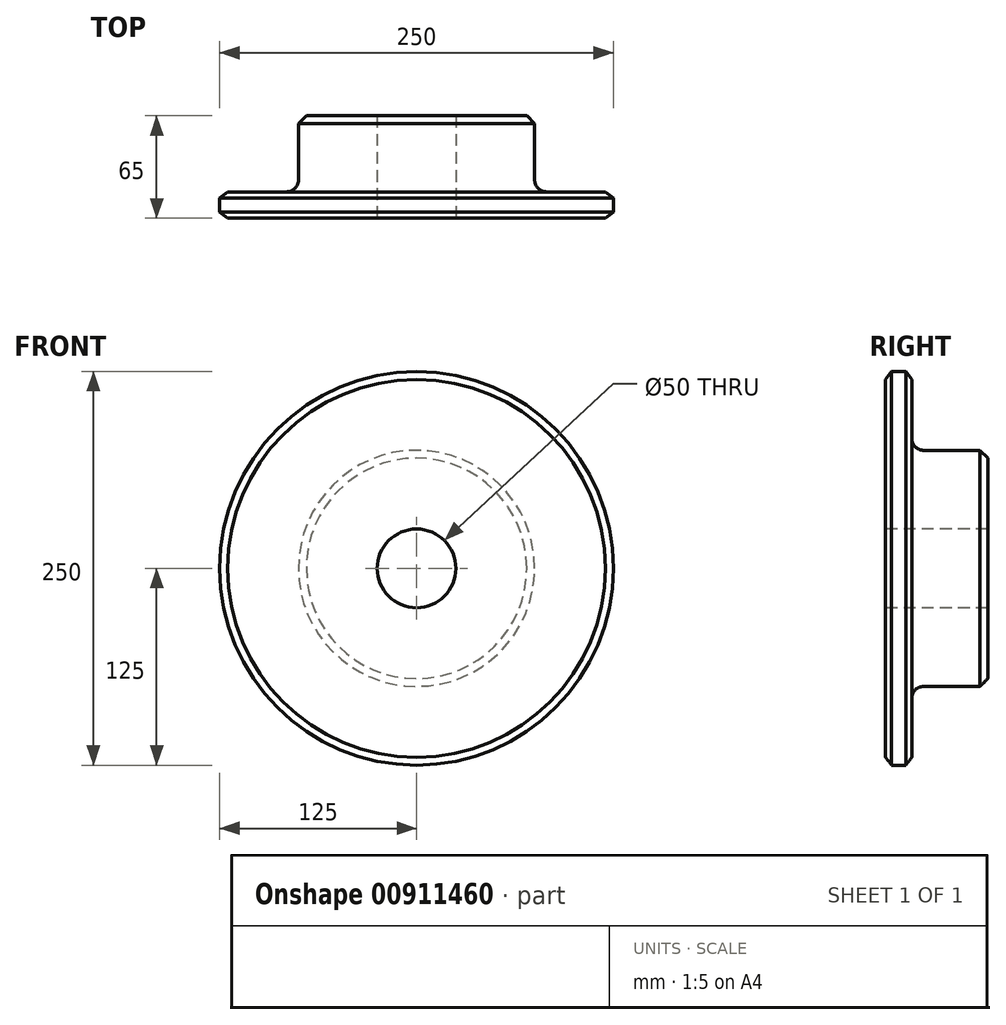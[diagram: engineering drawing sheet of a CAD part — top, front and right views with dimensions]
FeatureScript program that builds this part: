
annotation { "Feature Type Name" : "Feature", "Feature Type Description" : "" }
export const myFeature = defineFeature(function(context is Context, id is Id, definition is map)
    precondition{}
    {
        {
            var Q0;
            Q0=qCreatedBy(makeId("Right.planeOp"),FACE);
            var sketch = newSketch(context, id + "F0", { "sketchPlane" : qUnion([Q0])});
            skLineSegment(sketch, "E0", {"start": v(0, 0) * mm, "end": v(65, 0) * mm, "construction": true});
            skLineSegment(sketch, "E1.bottom", {"start": v(0, 25) * mm, "end": v(16.67, 25) * mm});
            skLineSegment(sketch, "E1.top", {"start": v(0, 125) * mm, "end": v(16.67, 125) * mm});
            skLineSegment(sketch, "E1.left", {"start": v(0, 25) * mm, "end": v(0, 125) * mm});
            skLineSegment(sketch, "E1.right", {"start": v(16.67, 25) * mm, "end": v(16.67, 125) * mm});
            skLineSegment(sketch, "E2.bottom", {"start": v(0, 25) * mm, "end": v(65, 25) * mm});
            skLineSegment(sketch, "E2.top", {"start": v(0, 75) * mm, "end": v(65, 75) * mm});
            skLineSegment(sketch, "E2.left", {"start": v(0, 25) * mm, "end": v(0, 75) * mm});
            skLineSegment(sketch, "E2.right", {"start": v(65, 25) * mm, "end": v(65, 75) * mm});
            skLineSegment(sketch, "E3.MirrorCS", {"start": v(0, -25) * mm, "end": v(16.67, -25) * mm});
            skLineSegment(sketch, "E4.MirrorCS", {"start": v(65, -25) * mm, "end": v(65, -75) * mm});
            skLineSegment(sketch, "E5.MirrorCS", {"start": v(0, -25) * mm, "end": v(65, -25) * mm});
            skLineSegment(sketch, "E6.MirrorCS", {"start": v(0, -25) * mm, "end": v(0, -75) * mm});
            skLineSegment(sketch, "E7.MirrorCS", {"start": v(0, -75) * mm, "end": v(65, -75) * mm});
            skLineSegment(sketch, "E8.MirrorCS", {"start": v(0, -25) * mm, "end": v(0, -125) * mm});
            skLineSegment(sketch, "E9.MirrorCS", {"start": v(16.67, -25) * mm, "end": v(16.67, -125) * mm});
            skLineSegment(sketch, "E10.MirrorCS", {"start": v(0, -125) * mm, "end": v(16.67, -125) * mm});
            skSolve(sketch);
        }
        {
            var Q0;
            {var subQ0=sQuery(id+"F0.wireOp",EDGE,"E1.top");Q0=makeQuery(id+"F0.imprint","IMPRINT",FACE,{"disambiguationData":[TD([[makeQuery(id+"F0.imprint","IMPRINT",EDGE,{"derivedFrom":subQ0}),-1.0]])]});}
            var Q1;
            {var subQ0=sQuery(id+"F0.wireOp",EDGE,"E1.bottom");Q1=makeQuery(id+"F0.imprint","IMPRINT",FACE,{"disambiguationData":[TD([[makeQuery(id+"F0.imprint","IMPRINT",EDGE,{"derivedFrom":subQ0}),1.0]])]});}
            var Q2;
            {var subQ0=sQuery(id+"F0.wireOp",EDGE,"E2.bottom");Q2=makeQuery(id+"F0.imprint","IMPRINT",FACE,{"disambiguationData":[TD([[makeQuery(id+"F0.imprint","IMPRINT",EDGE,{"derivedFrom":subQ0}),1.0]])]});}
            var Q3;
            Q3=sQuery(id+"F0.wireOp",EDGE,"E0");
            revolve(context, id + "F1", {"surfaceOperationType" : NewSurfaceOperationType.NEW, "entities" : qUnion([Q0, Q1, Q2]), "axis" : qUnion([Q3]), "revolveType" : RevolveType.FULL});
        }
        {
            var Q0;
            Q0=makeQuery(id+"F1.opRevolve","SWEPT_EDGE",EDGE,{"disambiguationData":[OSD([sQuery(id+"F0.wireOp",EDGE,"E1.right"),sQuery(id+"F0.wireOp",EDGE,"E2.top")])]});
            fillet(context, id + "F2", {"entities" : qUnion([Q0]), "radius" : 7.5 * mm, "tangentPropagation" : true, "allowEdgeOverflow" : false});
        }
        {
            var Q0;
            Q0=makeQuery(id+"F1.opRevolve","SWEPT_EDGE",EDGE,{"disambiguationData":[OSD([sQuery(id+"F0.wireOp",EDGE,"E2.top"),sQuery(id+"F0.wireOp",EDGE,"E2.right")])]});
            chamfer(context, id + "F3", {"entities" : qUnion([Q0]), "width" : 5 * mm, "tangentPropagation" : true});
        }
        {
            var Q0;
            Q0=makeQuery(id+"F1.opRevolve","SWEPT_EDGE",EDGE,{"disambiguationData":[OSD([sQuery(id+"F0.wireOp",EDGE,"E1.top"),sQuery(id+"F0.wireOp",EDGE,"E1.left")])]});
            var Q1;
            Q1=makeQuery(id+"F1.opRevolve","SWEPT_EDGE",EDGE,{"disambiguationData":[OSD([sQuery(id+"F0.wireOp",EDGE,"E1.top"),sQuery(id+"F0.wireOp",EDGE,"E1.right")])]});
            chamfer(context, id + "F4", {"entities" : qUnion([Q0, Q1]), "chamferType" : ChamferType.TWO_OFFSETS, "width1" : 5 * mm, "oppositeDirection" : false, "width2" : 3.8 * mm, "tangentPropagation" : true});
        }
    });
